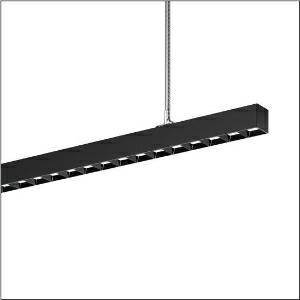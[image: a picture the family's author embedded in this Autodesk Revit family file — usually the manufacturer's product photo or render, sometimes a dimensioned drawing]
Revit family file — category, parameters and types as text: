
# Revit family: silica_r__21_51mx31tctdb_123f
name_source: partatom
category: Lighting Fixtures
units: mm (PartAtom-declared; Revit-internal decimal feet)

## family parameters
Cut with Voids When Loaded = No
Host = Face
Light Source = No
Part Type = Normal
Room Calculation Point = No
Round Connector Dimension = Use Diameter
Shared = No

## types (1)
- --- (1 x LED, 15550 lm, 133.9 W, 6500K)
    Apparent Load = 134 VA
    CIE Flux Codes = 85 99 100 60 100
    Color Rendering = 80
    Color Temperature = 6500K
    Default Elevation = 1800 mm
    Description = Silica® 21, office luminaire, primary light control with darklight reflector, of PMMA, black, CAT 2 (L<= 3000cd/m²), light emission: direct/indirect distribution, primary light characteristic: symmetric, installation type: suspended mounting, LED, rated luminous flux: 15.550lm, luminous efficacy: 111lm/W, light colour: 8tw, colour temperature: 2700..6500K, control gear: ECG DALI, with terminal, 3+2-pole, max. 2.5mm², mains connection: 220..240V, AC, 50/60Hz, rated input power: 140.6W, luminaire housing, of aluminium, jet black (RAL 9005), length: 3.004mm, width: 53mm, height: 53mm, protection rating (complete): IP20, insulation class (complete): insulation class I (protective earthing), certification: CE, permissible operating ambient temperature: 0..+35°C, standard: EN 50419, packaging unit: 1 piece
    Height = 53 mm
    Lamp = 1 x LED
    Lamp Light Flux = 15550 lm
    Lamp Power = 133.9 W
    Lamp count = 1
    Length = 3004 mm
    Luminous efficacy = 116 lm/W
    Manufacturer = Siteco
    ModVariant = No
    Model = 51MX31TCTDB
    Mounting Place = Ceiling
    Mounting Type = Pendant
    Number of Poles = 1
    OnlyDefault = Yes
    Power Factor = 1
    Product Name = Silica® 21
    Product group = office luminaire | ceiling pendant
    ProductGroupID = 905
    Protection Class = Protection class I
    Protection Degree = IP 20
    RLX_Detail_Level = 1
    RlxData = <blob elided: 64101 chars, md5=69c3b2eb>
    Socket = socket
    Standby Power = 0 W
    System Light Flux = 15550 lm
    System Power = 134 W
    Type Comments = individual setting
    Type Image = l_1251718.jpg
    URL = http://relux.com
    VarID = @adj_045969
    Voltage = 0 V
    Weight = 0.00 kg
    Width = 53 mm

## geometry (parser evidence)
native form markers: Blend x4, Sweep x13
no freeform markers — native parametric forms only
